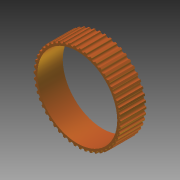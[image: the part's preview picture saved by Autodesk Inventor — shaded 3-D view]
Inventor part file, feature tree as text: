
AUTODESK INVENTOR PART (.ipt)
format: ipt  version: 2012 (Build 160160000, 160)  size: 281,600 bytes
history: native  units: in
note: dims shown in document units (in); Inventor stores cm internally (conversion verified against a paired STEP export)
features: extrude x1, sketch x1
ambient origin geometry x8: Origin, YZ Plane, XZ Plane, XY Plane, X Axis, Y Axis, Z Axis, Center Point
bodies: Solid1 (feature_tree)
feature tree (2):
  extrude  "Extrusion1"  Depth=1.5in
  sketch  "Sketch1"  dims[d0=2.75in d1=1.5in d3=19.685in d5=360.0deg d10=3.0in d11=0.875in d12=0.0in d17=0.0625in]
